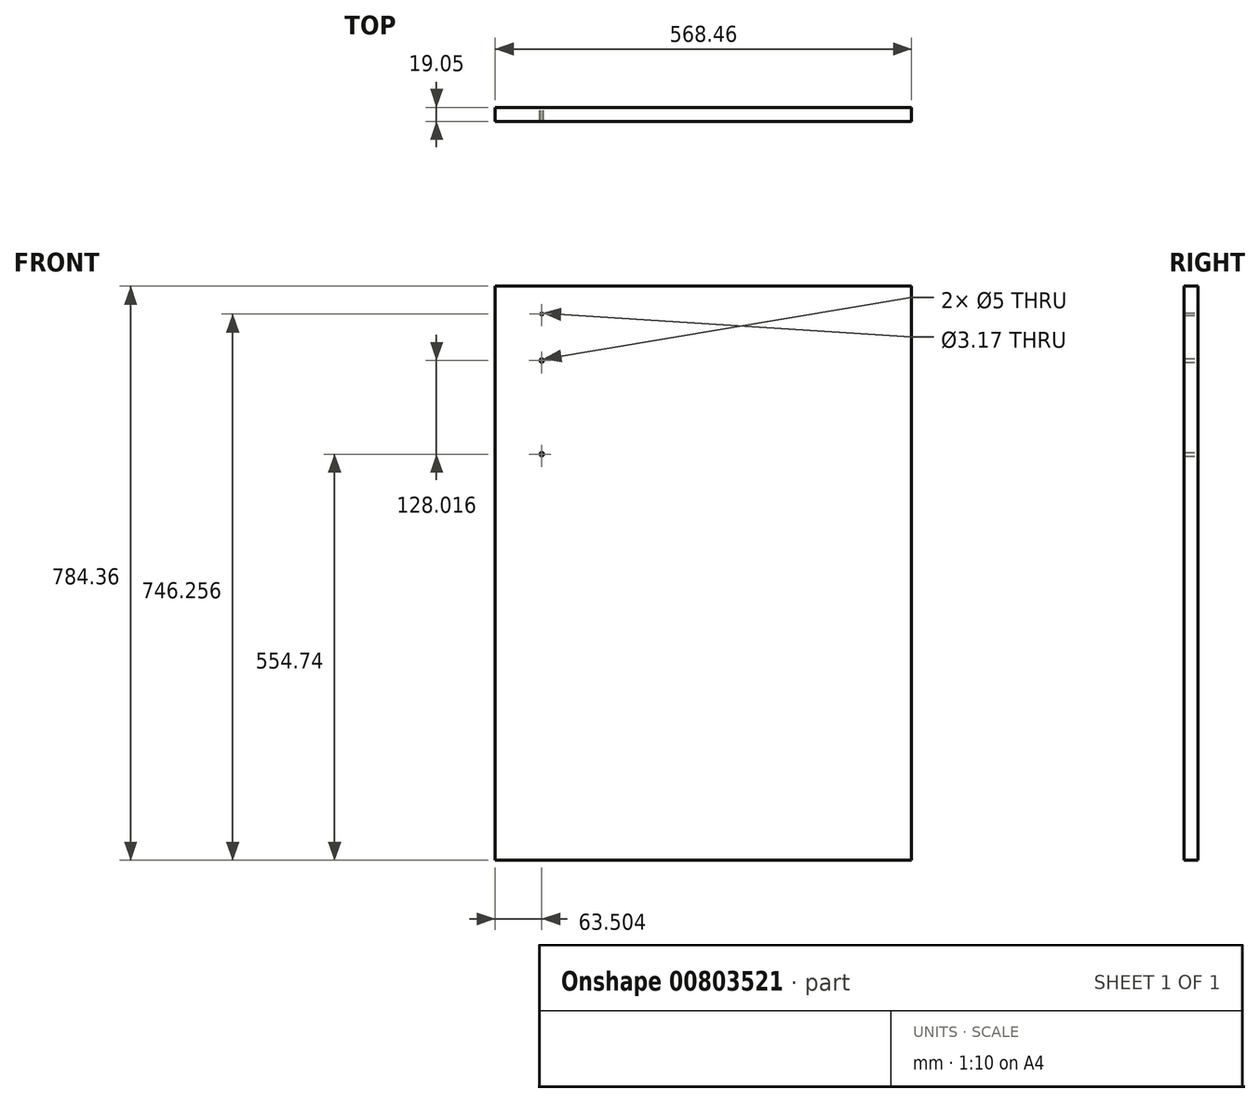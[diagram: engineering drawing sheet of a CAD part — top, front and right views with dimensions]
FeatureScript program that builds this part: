
annotation { "Feature Type Name" : "Feature", "Feature Type Description" : "" }
export const myFeature = defineFeature(function(context is Context, id is Id, definition is map)
    precondition{}
    {
        {
            var Q0;
            Q0=qCreatedBy(makeId("Front.planeOp"),FACE);
            var sketch = newSketch(context, id + "F0", { "sketchPlane" : qUnion([Q0])});
            skLineSegment(sketch, "E0.bottom", {"start": v(284.23, 392.18) * mm, "end": v(-284.23, 392.18) * mm});
            skLineSegment(sketch, "E0.top", {"start": v(284.23, -392.18) * mm, "end": v(-284.23, -392.18) * mm});
            skLineSegment(sketch, "E0.left", {"start": v(284.23, 392.18) * mm, "end": v(284.23, -392.18) * mm});
            skLineSegment(sketch, "E0.right", {"start": v(-284.23, 392.18) * mm, "end": v(-284.23, -392.18) * mm});
            skPoint(sketch, "E0.middle", {"position": v(0, 0) * mm});
            skSolve(sketch);
        }
        {
            var Q0;
            Q0=makeQuery(id+"F0.imprint","IMPRINT",FACE,{"disambiguationData":[TD([[makeQuery(id+"F0.imprint","IMPRINT",EDGE,{"derivedFrom":sQuery(id+"F0.wireOp",EDGE,"E0.bottom")}),1.0]])]});
            extrude(context, id + "F1", {"entities" : qUnion([Q0]), "depth" : 19.05 * mm, "offsetDistance" : 25.4 * mm});
        }
        {
            var Q0;
            Q0=makeQuery(id+"F1.opExtrude","CAP_FACE",FACE,{"disambiguationData":[OSD([sQuery(id+"F0.wireOp",EDGE,"E0.bottom"),sQuery(id+"F0.wireOp",EDGE,"E0.top"),sQuery(id+"F0.wireOp",EDGE,"E0.left"),sQuery(id+"F0.wireOp",EDGE,"E0.right")])],"isStart":false});
            var sketch = newSketch(context, id + "F2", { "sketchPlane" : qUnion([Q0])});
            skLineSegment(sketch, "E1", {"start": v(-284.23, 392.18) * mm, "end": v(-220.73, 392.18) * mm});
            skLineSegment(sketch, "E2", {"start": v(-220.73, 392.18) * mm, "end": v(-220.73, 290.58) * mm});
            skLineSegment(sketch, "E3", {"start": v(-220.73, 290.58) * mm, "end": v(-220.73, 162.56) * mm});
            skPoint(sketch, "E4", {"position": v(-220.73, 290.58) * mm});
            skPoint(sketch, "E5", {"position": v(-220.73, 162.56) * mm});
            skSolve(sketch);
        }
        {
            var Q0;
            Q0=sQuery(id+"F2.wireOp",VERTEX,"E4");
            var Q1;
            Q1=sQuery(id+"F2.wireOp",VERTEX,"E5");
            var Q2;
            Q2=makeQuery(id+"F1.opExtrude","SWEPT_BODY",BODY,{"disambiguationData":[OSD([sQuery(id+"F0.wireOp",EDGE,"E0.bottom"),sQuery(id+"F0.wireOp",EDGE,"E0.top"),sQuery(id+"F0.wireOp",EDGE,"E0.left"),sQuery(id+"F0.wireOp",EDGE,"E0.right")])]});
            hole(context, id + "F3", {"style" : HoleStyle.SIMPLE, "endStyle" : HoleEndStyle.BLIND, "holeDiameter" : 5 * mm, "majorDiameter" : 6.35 * mm, "holeDepth" : 25.4 * mm, "isTappedThrough" : true, "tappedDepth" : 12.7 * mm, "tapClearance" : 3, "startFromSketch" : true, "locations" : qUnion([Q0, Q1]), "scope" : qUnion([Q2])});
        }
        {
            var Q0;
            Q0=makeQuery(id+"F1.opExtrude","CAP_FACE",FACE,{"disambiguationData":[OSD([sQuery(id+"F0.wireOp",EDGE,"E0.bottom"),sQuery(id+"F0.wireOp",EDGE,"E0.top"),sQuery(id+"F0.wireOp",EDGE,"E0.left"),sQuery(id+"F0.wireOp",EDGE,"E0.right")])],"isStart":false});
            var sketch = newSketch(context, id + "F4", { "sketchPlane" : qUnion([Q0])});
            skLineSegment(sketch, "E6", {"start": v(-284.23, 392.18) * mm, "end": v(-220.73, 392.18) * mm});
            skLineSegment(sketch, "E7", {"start": v(-220.73, 392.18) * mm, "end": v(-220.73, 354.08) * mm});
            skSolve(sketch);
        }
        {
            var Q0;
            Q0=sQuery(id+"F4.wireOp",VERTEX,"E7.end");
            var Q1;
            Q1=makeQuery(id+"F1.opExtrude","SWEPT_BODY",BODY,{"disambiguationData":[OSD([sQuery(id+"F0.wireOp",EDGE,"E0.bottom"),sQuery(id+"F0.wireOp",EDGE,"E0.top"),sQuery(id+"F0.wireOp",EDGE,"E0.left"),sQuery(id+"F0.wireOp",EDGE,"E0.right")])]});
            hole(context, id + "F5", {"style" : HoleStyle.SIMPLE, "endStyle" : HoleEndStyle.BLIND, "holeDiameter" : 3.17 * mm, "majorDiameter" : 6.35 * mm, "holeDepth" : 25.4 * mm, "isTappedThrough" : true, "tappedDepth" : 12.7 * mm, "tapClearance" : 3, "startFromSketch" : true, "locations" : qUnion([Q0]), "scope" : qUnion([Q1])});
        }
    });
